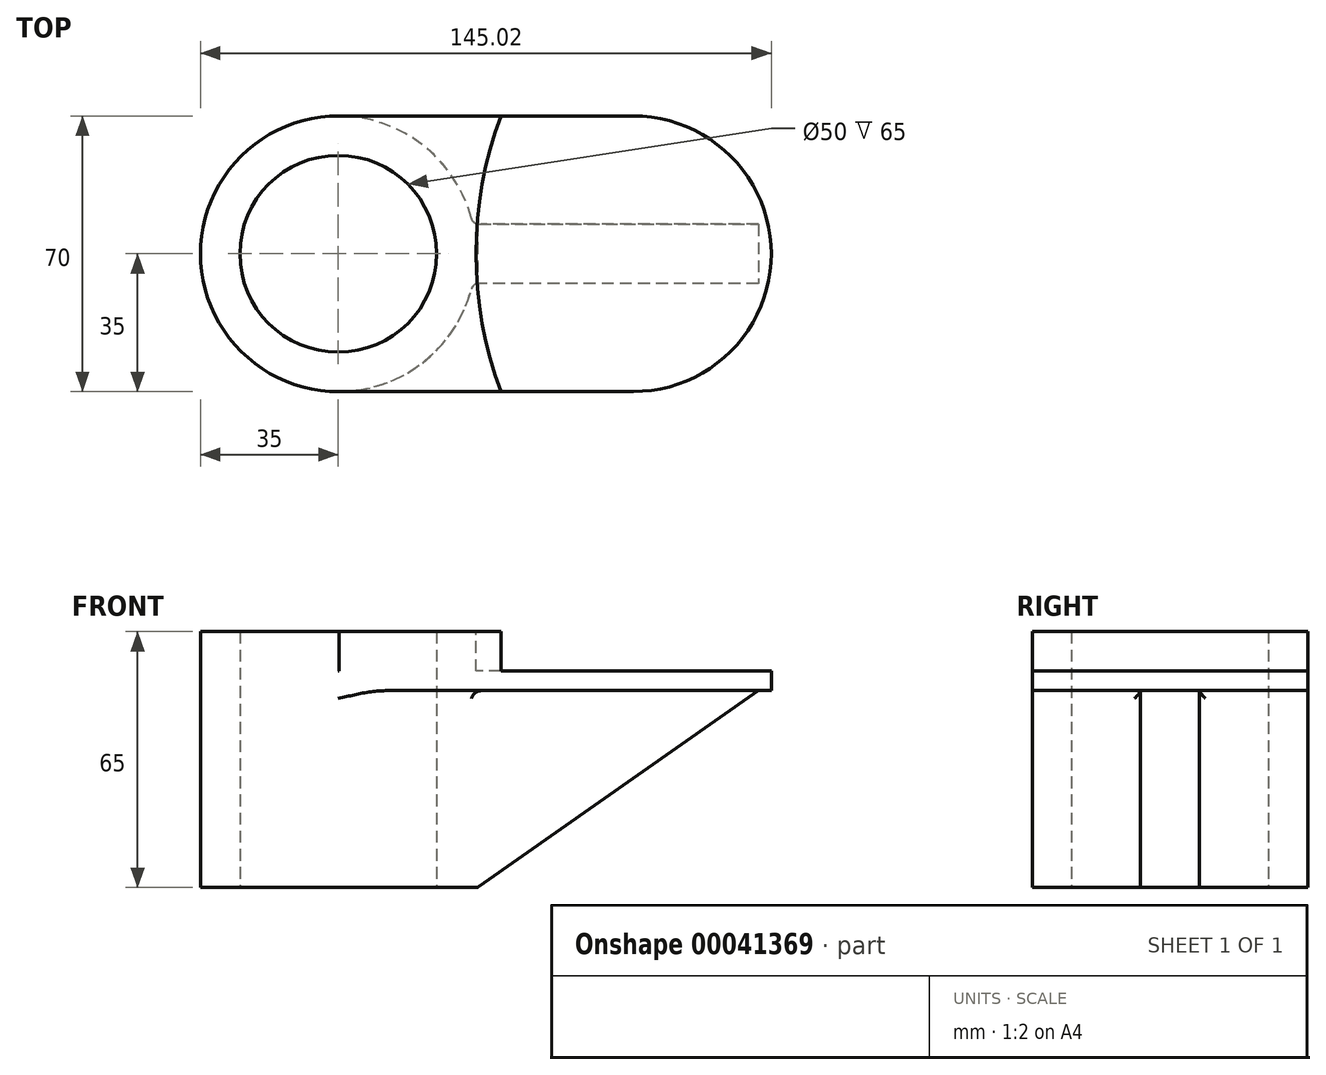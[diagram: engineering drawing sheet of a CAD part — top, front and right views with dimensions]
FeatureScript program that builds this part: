
annotation { "Feature Type Name" : "Feature", "Feature Type Description" : "" }
export const myFeature = defineFeature(function(context is Context, id is Id, definition is map)
    precondition{}
    {
        {
            var Q0;
            Q0=qCreatedBy(makeId("Top.planeOp"),FACE);
            var sketch = newSketch(context, id + "F0", { "sketchPlane" : qUnion([Q0])});
            skCircle(sketch, "E0", {"center": v(0, 0) * mm, "radius": 35 * mm});
            skSolve(sketch);
        }
        {
            var Q0;
            Q0=makeQuery(id+"F0.imprint","IMPRINT",FACE,{"disambiguationData":[TD([[makeQuery(id+"F0.imprint","IMPRINT",EDGE,{"derivedFrom":sQuery(id+"F0.wireOp",EDGE,"E0")}),1.0]])]});
            extrude(context, id + "F1", {"entities" : qUnion([Q0]), "depth" : 15 * mm, "hasSecondDirection" : true, "secondDirectionOppositeDirection" : true, "secondDirectionDepth" : 50 * mm});
        }
        {
            var Q0;
            Q0=qCreatedBy(makeId("Top.planeOp"),FACE);
            var sketch = newSketch(context, id + "F2", { "sketchPlane" : qUnion([Q0])});
            skLineSegment(sketch, "E1.rect.bottom", {"start": v(75, 35) * mm, "end": v(0, 35) * mm});
            skLineSegment(sketch, "E1.rect.top", {"start": v(75, -35) * mm, "end": v(0, -35) * mm});
            skLineSegment(sketch, "E1.rect.left", {"start": v(75, 35) * mm, "end": v(75, -35) * mm});
            skLineSegment(sketch, "E1.rect.right", {"start": v(0, 35) * mm, "end": v(0, -35) * mm});
            skPoint(sketch, "E1.rect.middle", {"position": v(37.5, 0) * mm});
            skSolve(sketch);
        }
        {
            var Q0;
            Q0=qCreatedBy(makeId("Top.planeOp"),FACE);
            var sketch = newSketch(context, id + "F3", { "sketchPlane" : qUnion([Q0])});
            skCircle(sketch, "E2", {"center": v(75.02, 0) * mm, "radius": 35 * mm});
            skSolve(sketch);
        }
        {
            var Q0;
            Q0=makeQuery(id+"F3.imprint","IMPRINT",FACE,{"disambiguationData":[TD([[makeQuery(id+"F3.imprint","IMPRINT",EDGE,{"derivedFrom":sQuery(id+"F3.wireOp",EDGE,"E2")}),1.0]])]});
            var Q1;
            Q1=makeQuery(id+"F2.imprint","IMPRINT",FACE,{"disambiguationData":[TD([[makeQuery(id+"F2.imprint","IMPRINT",EDGE,{"derivedFrom":sQuery(id+"F2.wireOp",EDGE,"E1.rect.bottom")}),1.0]])]});
            extrude(context, id + "F4", {"entities" : qUnion([Q0, Q1]), "operationType" : NewBodyOperationType.ADD, "depth" : 5 * mm});
        }
        {
            var Q0;
            Q0=makeQuery(id+"F4.boolean.opBoolean","MERGE",FACE,{"derivedFrom":[makeQuery(id+"F4.opExtrude","CAP_FACE",FACE,{"disambiguationData":[OSD([sQuery(id+"F2.wireOp",EDGE,"E1.rect.bottom"),sQuery(id+"F2.wireOp",EDGE,"E1.rect.top"),sQuery(id+"F2.wireOp",EDGE,"E1.rect.left"),sQuery(id+"F2.wireOp",EDGE,"E1.rect.right")])],"isStart":false}),makeQuery(id+"F4.opExtrude","CAP_FACE",FACE,{"disambiguationData":[OSD([sQuery(id+"F3.wireOp",EDGE,"E2")])],"isStart":false})]});
            var sketch = newSketch(context, id + "F5", { "sketchPlane" : qUnion([Q0])});
            skLineSegment(sketch, "E3.rect.bottom", {"start": v(57.08, -35) * mm, "end": v(0.17, -35) * mm});
            skLineSegment(sketch, "E3.rect.top", {"start": v(57.08, 35) * mm, "end": v(0.17, 35) * mm});
            skLineSegment(sketch, "E3.rect.left", {"start": v(57.08, -35) * mm, "end": v(57.08, 35) * mm});
            skLineSegment(sketch, "E3.rect.right", {"start": v(0.17, -35) * mm, "end": v(0.17, 35) * mm});
            skPoint(sketch, "E3.rect.middle", {"position": v(28.62, 0) * mm});
            skSolve(sketch);
        }
        {
            var Q0;
            Q0=qSketchRegion(id+"F5",true);
            extrude(context, id + "F6", {"entities" : qUnion([Q0]), "operationType" : NewBodyOperationType.ADD, "depth" : 10 * mm});
        }
        {
            var Q0;
            Q0=makeQuery(id+"F6.boolean.opBoolean","MERGE",FACE,{"derivedFrom":[makeQuery(id+"F1.opExtrude","CAP_FACE",FACE,{"disambiguationData":[OSD([sQuery(id+"F0.wireOp",EDGE,"E0")])],"isStart":false}),makeQuery(id+"F6.opExtrude","CAP_FACE",FACE,{"disambiguationData":[OSD([sQuery(id+"F5.wireOp",EDGE,"E3.rect.bottom"),sQuery(id+"F5.wireOp",EDGE,"E3.rect.top"),sQuery(id+"F5.wireOp",EDGE,"E3.rect.left"),sQuery(id+"F5.wireOp",EDGE,"E3.rect.right")])],"isStart":false})]});
            var sketch = newSketch(context, id + "F7", { "sketchPlane" : qUnion([Q0])});
            skCircle(sketch, "E4", {"center": v(135, 0) * mm, "radius": 100 * mm});
            skSolve(sketch);
        }
        {
            var Q0;
            {var subQ3=makeQuery(id+"F6.opExtrude","CAP_EDGE",EDGE,{"disambiguationData":[OSD([sQuery(id+"F5.wireOp",EDGE,"E3.rect.left")])],"isStart":false});Q0=makeQuery(id+"F7.imprint","IMPRINT",FACE,{"disambiguationData":[TD([[makeQuery(id+"F7.imprint","IMPRINT",EDGE,{"derivedFrom":subQ3}),1.0]])]});}
            extrude(context, id + "F8", {"entities" : qUnion([Q0]), "operationType" : NewBodyOperationType.REMOVE, "oppositeDirection" : true, "depth" : 10 * mm});
        }
        {
            var Q0;
            Q0=makeQuery(id+"F3.imprint","IMPRINT",FACE,{"disambiguationData":[TD([[makeQuery(id+"F3.imprint","IMPRINT",EDGE,{"derivedFrom":sQuery(id+"F3.wireOp",EDGE,"E2")}),1.0]])]});
            var sketch = newSketch(context, id + "F9", { "sketchPlane" : qUnion([Q0])});
            skLineSegment(sketch, "E5.rect.bottom", {"start": v(108.34, 7.5) * mm, "end": v(8.34, 7.5) * mm});
            skLineSegment(sketch, "E5.rect.top", {"start": v(108.34, -7.5) * mm, "end": v(8.34, -7.5) * mm});
            skLineSegment(sketch, "E5.rect.left", {"start": v(108.34, 7.5) * mm, "end": v(108.34, -7.5) * mm});
            skLineSegment(sketch, "E5.rect.right", {"start": v(8.34, 7.5) * mm, "end": v(8.34, -7.5) * mm});
            skPoint(sketch, "E5.rect.middle", {"position": v(58.34, 0) * mm});
            skSolve(sketch);
        }
        {
            var Q0;
            Q0=qSketchRegion(id+"F9",true);
            extrude(context, id + "F10", {"entities" : qUnion([Q0]), "operationType" : NewBodyOperationType.ADD, "oppositeDirection" : true, "depth" : 50 * mm});
        }
        {
            var Q0;
            Q0=makeQuery(id+"F10.opExtrude","CAP_EDGE",EDGE,{"disambiguationData":[OSD([sQuery(id+"F9.wireOp",EDGE,"E5.rect.left")])],"isStart":false});
            chamfer(context, id + "F11", {"entities" : qUnion([Q0]), "chamferType" : ChamferType.OFFSET_ANGLE, "width" : 73 * mm, "oppositeDirection" : false, "angle" : 35 * degree, "tangentPropagation" : true});
        }
        {
            var Q0;
            Q0=makeQuery(id+"F10.boolean.opBoolean","MERGE",FACE,{"derivedFrom":[makeQuery(id+"F1.opExtrude","CAP_FACE",FACE,{"disambiguationData":[OSD([sQuery(id+"F0.wireOp",EDGE,"E0")])],"isStart":true}),makeQuery(id+"F10.opExtrude","CAP_FACE",FACE,{"disambiguationData":[OSD([sQuery(id+"F9.wireOp",EDGE,"E5.rect.bottom"),sQuery(id+"F9.wireOp",EDGE,"E5.rect.top"),sQuery(id+"F9.wireOp",EDGE,"E5.rect.left"),sQuery(id+"F9.wireOp",EDGE,"E5.rect.right")])],"isStart":false})]});
            var sketch = newSketch(context, id + "F12", { "sketchPlane" : qUnion([Q0])});
            skCircle(sketch, "E6", {"center": v(0, 0) * mm, "radius": 25 * mm});
            skSolve(sketch);
        }
        {
            var Q0;
            Q0=makeQuery(id+"F12.imprint","IMPRINT",FACE,{"disambiguationData":[TD([[makeQuery(id+"F12.imprint","IMPRINT",EDGE,{"derivedFrom":sQuery(id+"F12.wireOp",EDGE,"E6")}),1.0]])]});
            extrude(context, id + "F13", {"entities" : qUnion([Q0]), "operationType" : NewBodyOperationType.REMOVE, "endBound" : BoundingType.THROUGH_ALL, "oppositeDirection" : true, "depth" : 25.4 * mm});
        }
        {
            var Q0;
            Q0=makeQuery(id+"F10.opExtrude","CAP_EDGE",EDGE,{"disambiguationData":[OSD([sQuery(id+"F9.wireOp",EDGE,"E5.rect.top")])],"isStart":true});
            var Q1;
            Q1=makeQuery(id+"F10.opExtrude","CAP_EDGE",EDGE,{"disambiguationData":[OSD([sQuery(id+"F9.wireOp",EDGE,"E5.rect.bottom")])],"isStart":true});
            var Q2;
            Q2=makeQuery(id+"F10.boolean.opBoolean","INTERSECT",EDGE,{"derivedFrom":[makeQuery(id+"F1.opExtrude","SWEPT_FACE",FACE,{"disambiguationData":[OSD([sQuery(id+"F0.wireOp",EDGE,"E0")])]}),makeQuery(id+"F10.opExtrude","SWEPT_FACE",FACE,{"disambiguationData":[OSD([sQuery(id+"F9.wireOp",EDGE,"E5.rect.top")])]})]});
            var Q3;
            Q3=makeQuery(id+"F10.boolean.opBoolean","INTERSECT",EDGE,{"derivedFrom":[makeQuery(id+"F1.opExtrude","SWEPT_FACE",FACE,{"disambiguationData":[OSD([sQuery(id+"F0.wireOp",EDGE,"E0")])]}),makeQuery(id+"F10.opExtrude","SWEPT_FACE",FACE,{"disambiguationData":[OSD([sQuery(id+"F9.wireOp",EDGE,"E5.rect.bottom")])]})]});
            var Q4;
            {var subQ0=makeQuery(id+"F1.opExtrude","SWEPT_FACE",FACE,{"disambiguationData":[OSD([sQuery(id+"F0.wireOp",EDGE,"E0")])]});var subQ1=sQuery(id+"F2.wireOp",EDGE,"E1.rect.top");var subQ2=makeQuery(id+"F4.opExtrude","CAP_FACE",FACE,{"disambiguationData":[OSD([sQuery(id+"F2.wireOp",EDGE,"E1.rect.bottom"),subQ1,sQuery(id+"F2.wireOp",EDGE,"E1.rect.left"),sQuery(id+"F2.wireOp",EDGE,"E1.rect.right")])],"isStart":true});var subQ3=makeQuery(id+"F4.opExtrude","CAP_FACE",FACE,{"disambiguationData":[OSD([sQuery(id+"F3.wireOp",EDGE,"E2")])],"isStart":true});Q4=makeQuery(id+"F10.boolean.opBoolean","SPLIT",EDGE,{"disambiguationData":[TD([makeQuery(id+"F4.opExtrude","SWEPT_FACE",FACE,{"disambiguationData":[OSD([subQ1])]})])],"derivedFrom":makeQuery(id+"F4.boolean.opBoolean","INTERSECT",EDGE,{"derivedFrom":[subQ0,subQ2,subQ3]})});}
            var Q5;
            {var subQ0=makeQuery(id+"F1.opExtrude","SWEPT_FACE",FACE,{"disambiguationData":[OSD([sQuery(id+"F0.wireOp",EDGE,"E0")])]});var subQ1=sQuery(id+"F2.wireOp",EDGE,"E1.rect.bottom");var subQ2=makeQuery(id+"F4.opExtrude","CAP_FACE",FACE,{"disambiguationData":[OSD([subQ1,sQuery(id+"F2.wireOp",EDGE,"E1.rect.top"),sQuery(id+"F2.wireOp",EDGE,"E1.rect.left"),sQuery(id+"F2.wireOp",EDGE,"E1.rect.right")])],"isStart":true});var subQ3=makeQuery(id+"F4.opExtrude","CAP_FACE",FACE,{"disambiguationData":[OSD([sQuery(id+"F3.wireOp",EDGE,"E2")])],"isStart":true});Q5=makeQuery(id+"F10.boolean.opBoolean","SPLIT",EDGE,{"disambiguationData":[TD([makeQuery(id+"F4.opExtrude","SWEPT_FACE",FACE,{"disambiguationData":[OSD([subQ1])]})])],"derivedFrom":makeQuery(id+"F4.boolean.opBoolean","INTERSECT",EDGE,{"derivedFrom":[subQ0,subQ2,subQ3]})});}
            fillet(context, id + "F14", {"entities" : qUnion([Q0, Q1, Q2, Q3, Q4, Q5]), "radius" : 2 * mm, "tangentPropagation" : true, "allowEdgeOverflow" : false});
        }
    });
